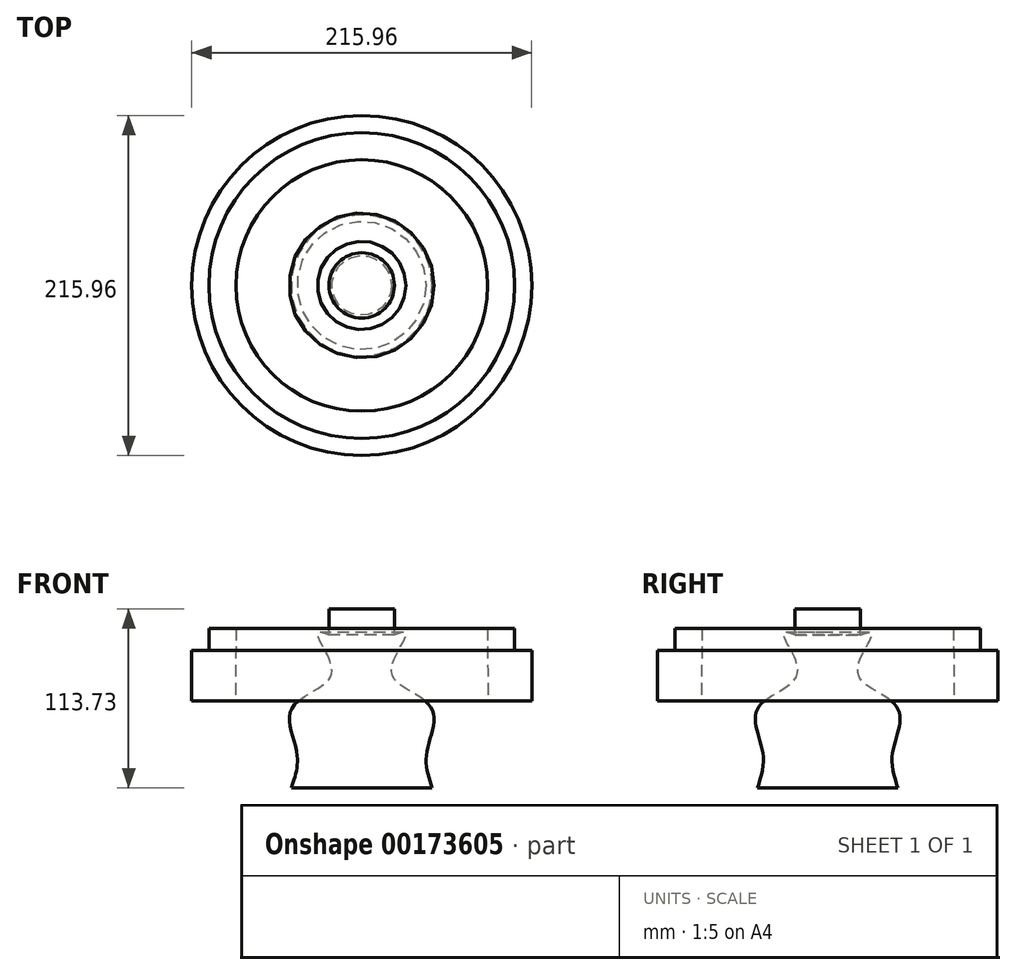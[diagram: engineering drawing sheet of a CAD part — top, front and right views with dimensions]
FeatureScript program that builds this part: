
annotation { "Feature Type Name" : "Feature", "Feature Type Description" : "" }
export const myFeature = defineFeature(function(context is Context, id is Id, definition is map)
    precondition{}
    {
        {
            var Q0;
            Q0=qCreatedBy(makeId("Front.planeOp"),FACE);
            var sketch = newSketch(context, id + "F0", { "sketchPlane" : qUnion([Q0])});
            skLineSegment(sketch, "E0", {"start": v(0, 36.9) * mm, "end": v(0, -50) * mm});
            skLineSegment(sketch, "E1", {"start": v(0, -50) * mm, "end": v(44.73, -50) * mm});
            skFitSpline(sketch, "E2", {"points": [v(44.73, -50) * mm, v(41.21, -27.63) * mm, v(44.73, 0) * mm, v(21.09, 18.69) * mm, v(22.04, 34.98) * mm, v(27.8, 48.4) * mm, v(0, 36.9) * mm], "startDerivative": vector(-43.67, 127.9) * mm, "endDerivative": vector(-205.1, -109.1) * mm});
            skLineSegment(sketch, "E3", {"start": v(0, 36.9) * mm, "end": v(0, 63.73) * mm});
            skLineSegment(sketch, "E4", {"start": v(0, 63.73) * mm, "end": v(20.77, 63.73) * mm});
            skLineSegment(sketch, "E5", {"start": v(20.77, 63.73) * mm, "end": v(20.77, 47.26) * mm});
            skLineSegment(sketch, "E6", {"start": v(79.87, 51.28) * mm, "end": v(97.12, 51.28) * mm});
            skLineSegment(sketch, "E7", {"start": v(97.12, 51.28) * mm, "end": v(97.12, 37.54) * mm});
            skLineSegment(sketch, "E8", {"start": v(97.12, 37.54) * mm, "end": v(107.98, 37.54) * mm});
            skLineSegment(sketch, "E9", {"start": v(107.98, 37.54) * mm, "end": v(107.98, 5.27) * mm});
            skLineSegment(sketch, "E10", {"start": v(107.98, 5.27) * mm, "end": v(80.19, 5.27) * mm});
            skLineSegment(sketch, "E11", {"start": v(80.19, 5.27) * mm, "end": v(79.87, 51.28) * mm});
            skSolve(sketch);
        }
        {
            var Q0;
            {var subQ0=sQuery(id+"F0.wireOp",EDGE,"E0");Q0=makeQuery(id+"F0.imprint","IMPRINT",FACE,{"disambiguationData":[TD([[makeQuery(id+"F0.imprint","IMPRINT",EDGE,{"derivedFrom":subQ0}),1.0]])]});}
            var Q1;
            {var subQ0=sQuery(id+"F0.wireOp",EDGE,"E3");Q1=makeQuery(id+"F0.imprint","IMPRINT",FACE,{"disambiguationData":[TD([[makeQuery(id+"F0.imprint","IMPRINT",EDGE,{"derivedFrom":subQ0}),-1.0]])]});}
            var Q2;
            Q2=makeQuery(id+"F0.imprint","IMPRINT",FACE,{"disambiguationData":[TD([[makeQuery(id+"F0.imprint","IMPRINT",EDGE,{"derivedFrom":sQuery(id+"F0.wireOp",EDGE,"E6")}),-1.0]])]});
            var Q3;
            Q3=sQuery(id+"F0.wireOp",EDGE,"E0");
            revolve(context, id + "F1", {"entities" : qUnion([Q0, Q1, Q2]), "axis" : qUnion([Q3]), "revolveType" : RevolveType.FULL});
        }
    });
